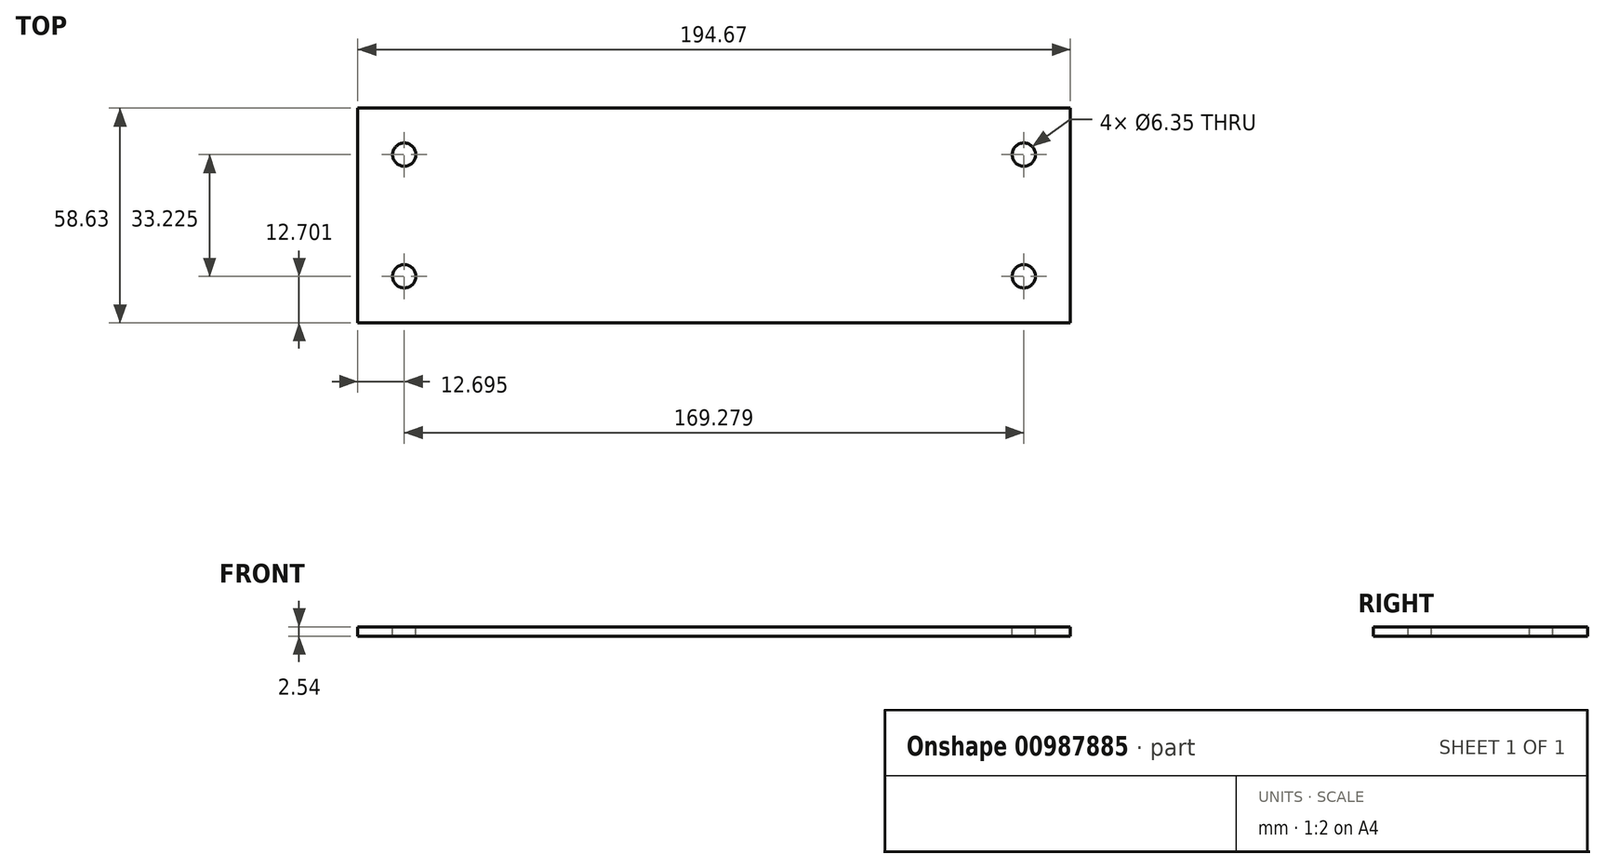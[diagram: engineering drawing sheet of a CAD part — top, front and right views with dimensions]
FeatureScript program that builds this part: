
annotation { "Feature Type Name" : "Feature", "Feature Type Description" : "" }
export const myFeature = defineFeature(function(context is Context, id is Id, definition is map)
    precondition{}
    {
        {
            var Q0;
            Q0=qCreatedBy(makeId("Top.planeOp"),FACE);
            var sketch = newSketch(context, id + "F0", { "sketchPlane" : qUnion([Q0])});
            skLineSegment(sketch, "E0.bottom", {"start": v(-83.6, 39.18) * mm, "end": v(111.07, 39.18) * mm});
            skLineSegment(sketch, "E0.top", {"start": v(-83.6, -19.45) * mm, "end": v(111.07, -19.45) * mm});
            skLineSegment(sketch, "E0.left", {"start": v(-83.6, 39.18) * mm, "end": v(-83.6, -19.45) * mm});
            skLineSegment(sketch, "E0.right", {"start": v(111.07, 39.18) * mm, "end": v(111.07, -19.45) * mm});
            skSolve(sketch);
        }
        {
            var Q0;
            Q0=makeQuery(id+"F0.imprint","IMPRINT",FACE,{"disambiguationData":[TD([[makeQuery(id+"F0.imprint","IMPRINT",EDGE,{"derivedFrom":sQuery(id+"F0.wireOp",EDGE,"E0.bottom")}),-1.0]])]});
            extrude(context, id + "F1", {"entities" : qUnion([Q0]), "depth" : 2.54 * mm, "offsetDistance" : 25.4 * mm});
        }
        {
            var Q0;
            Q0=makeQuery(id+"F1.opExtrude","CAP_FACE",FACE,{"disambiguationData":[OSD([sQuery(id+"F0.wireOp",EDGE,"E0.bottom"),sQuery(id+"F0.wireOp",EDGE,"E0.top"),sQuery(id+"F0.wireOp",EDGE,"E0.left"),sQuery(id+"F0.wireOp",EDGE,"E0.right")])],"isStart":false});
            var sketch = newSketch(context, id + "F2", { "sketchPlane" : qUnion([Q0])});
            skLineSegment(sketch, "E1.bottom", {"start": v(-83.6, 39.18) * mm, "end": v(-70.9, 39.18) * mm});
            skLineSegment(sketch, "E1.top", {"start": v(-83.6, -19.45) * mm, "end": v(-70.9, -19.45) * mm});
            skLineSegment(sketch, "E1.left", {"start": v(-83.6, 39.18) * mm, "end": v(-83.6, -19.45) * mm});
            skLineSegment(sketch, "E1.right", {"start": v(-70.9, 39.18) * mm, "end": v(-70.9, -19.45) * mm});
            skLineSegment(sketch, "E2.bottom", {"start": v(111.07, 39.18) * mm, "end": v(98.37, 39.18) * mm});
            skLineSegment(sketch, "E2.top", {"start": v(111.07, -19.45) * mm, "end": v(98.37, -19.45) * mm});
            skLineSegment(sketch, "E2.left", {"start": v(111.07, 39.18) * mm, "end": v(111.07, -19.45) * mm});
            skLineSegment(sketch, "E2.right", {"start": v(98.37, 39.18) * mm, "end": v(98.37, -19.45) * mm});
            skLineSegment(sketch, "E3.bottom", {"start": v(-83.6, 39.18) * mm, "end": v(111.07, 39.18) * mm});
            skLineSegment(sketch, "E3.top", {"start": v(-83.6, 26.48) * mm, "end": v(111.07, 26.48) * mm});
            skLineSegment(sketch, "E3.left", {"start": v(-83.6, 39.18) * mm, "end": v(-83.6, 26.48) * mm});
            skLineSegment(sketch, "E3.right", {"start": v(111.07, 39.18) * mm, "end": v(111.07, 26.48) * mm});
            skLineSegment(sketch, "E4.bottom", {"start": v(-83.6, -19.45) * mm, "end": v(111.07, -19.45) * mm});
            skLineSegment(sketch, "E4.top", {"start": v(-83.6, -6.75) * mm, "end": v(111.07, -6.75) * mm});
            skLineSegment(sketch, "E4.left", {"start": v(-83.6, -19.45) * mm, "end": v(-83.6, -6.75) * mm});
            skLineSegment(sketch, "E4.right", {"start": v(111.07, -19.45) * mm, "end": v(111.07, -6.75) * mm});
            skCircle(sketch, "E5", {"center": v(-70.9, -6.75) * mm, "radius": 3.18 * mm});
            skCircle(sketch, "E6", {"center": v(-70.9, 26.48) * mm, "radius": 3.18 * mm});
            skCircle(sketch, "E7", {"center": v(98.37, 26.48) * mm, "radius": 3.18 * mm});
            skCircle(sketch, "E8", {"center": v(98.37, -6.75) * mm, "radius": 3.18 * mm});
            skLineSegment(sketch, "E9", {"start": v(13.73, 39.18) * mm, "end": v(13.73, -19.45) * mm});
            skLineSegment(sketch, "E10", {"start": v(-83.6, 9.86) * mm, "end": v(111.07, 9.86) * mm});
            skLineSegment(sketch, "E11", {"start": v(13.73, 9.86) * mm, "end": v(45.48, 9.86) * mm});
            skLineSegment(sketch, "E12", {"start": v(45.48, 9.86) * mm, "end": v(45.48, 35.26) * mm});
            skLineSegment(sketch, "E13", {"start": v(45.48, 35.26) * mm, "end": v(-18.02, 35.26) * mm});
            skLineSegment(sketch, "E14", {"start": v(-18.02, 35.26) * mm, "end": v(-18.02, 0) * mm});
            skLineSegment(sketch, "E15", {"start": v(45.48, 9.86) * mm, "end": v(45.48, -15.54) * mm});
            skLineSegment(sketch, "E16", {"start": v(45.48, -15.54) * mm, "end": v(-18.02, -15.54) * mm});
            skLineSegment(sketch, "E17", {"start": v(-18.02, -15.54) * mm, "end": v(-18.02, 35.26) * mm});
            skSolve(sketch);
        }
        {
            var Q0;
            {var subQ0=sQuery(id+"F2.wireOp",EDGE,"E6");var subQ1=sQuery(id+"F2.wireOp",EDGE,"E1.right");var subQ2=makeQuery(id+"F2.imprint","INTERSECT",VERTEX,{"disambiguationData":[OD(1.0)],"derivedFrom":[subQ1,subQ0]});Q0=makeQuery(id+"F2.imprint","IMPRINT",FACE,{"disambiguationData":[TD([[makeQuery(id+"F2.imprint","IMPRINT",EDGE,{"disambiguationData":[TD([[subQ2,-1.0]])],"derivedFrom":subQ1}),-1.0]])]});}
            var Q1;
            {var subQ0=sQuery(id+"F2.wireOp",EDGE,"E6");var subQ1=sQuery(id+"F2.wireOp",EDGE,"E1.right");var subQ2=makeQuery(id+"F2.imprint","INTERSECT",VERTEX,{"disambiguationData":[OD(1.0)],"derivedFrom":[subQ1,subQ0]});Q1=makeQuery(id+"F2.imprint","IMPRINT",FACE,{"disambiguationData":[TD([[makeQuery(id+"F2.imprint","IMPRINT",EDGE,{"disambiguationData":[TD([[subQ2,-1.0]])],"derivedFrom":subQ1}),1.0]])]});}
            var Q2;
            {var subQ0=sQuery(id+"F2.wireOp",EDGE,"E6");var subQ1=sQuery(id+"F2.wireOp",EDGE,"E1.right");var subQ2=makeQuery(id+"F2.imprint","INTERSECT",VERTEX,{"disambiguationData":[OD(0.0)],"derivedFrom":[subQ1,subQ0]});Q2=makeQuery(id+"F2.imprint","IMPRINT",FACE,{"disambiguationData":[TD([[makeQuery(id+"F2.imprint","IMPRINT",EDGE,{"disambiguationData":[TD([[subQ2,1.0]])],"derivedFrom":subQ1}),1.0]])]});}
            var Q3;
            {var subQ0=sQuery(id+"F2.wireOp",EDGE,"E6");var subQ1=sQuery(id+"F2.wireOp",EDGE,"E1.right");var subQ2=makeQuery(id+"F2.imprint","INTERSECT",VERTEX,{"disambiguationData":[OD(0.0)],"derivedFrom":[subQ1,subQ0]});Q3=makeQuery(id+"F2.imprint","IMPRINT",FACE,{"disambiguationData":[TD([[makeQuery(id+"F2.imprint","IMPRINT",EDGE,{"disambiguationData":[TD([[subQ2,1.0]])],"derivedFrom":subQ1}),-1.0]])]});}
            var Q4;
            {var subQ0=sQuery(id+"F2.wireOp",EDGE,"E5");var subQ1=sQuery(id+"F2.wireOp",EDGE,"E1.right");var subQ2=makeQuery(id+"F2.imprint","INTERSECT",VERTEX,{"disambiguationData":[OD(0.0)],"derivedFrom":[subQ1,subQ0]});Q4=makeQuery(id+"F2.imprint","IMPRINT",FACE,{"disambiguationData":[TD([[makeQuery(id+"F2.imprint","IMPRINT",EDGE,{"disambiguationData":[TD([[subQ2,-1.0]])],"derivedFrom":subQ1}),-1.0]])]});}
            var Q5;
            {var subQ0=sQuery(id+"F2.wireOp",EDGE,"E5");var subQ1=sQuery(id+"F2.wireOp",EDGE,"E1.right");var subQ2=makeQuery(id+"F2.imprint","INTERSECT",VERTEX,{"disambiguationData":[OD(0.0)],"derivedFrom":[subQ1,subQ0]});Q5=makeQuery(id+"F2.imprint","IMPRINT",FACE,{"disambiguationData":[TD([[makeQuery(id+"F2.imprint","IMPRINT",EDGE,{"disambiguationData":[TD([[subQ2,-1.0]])],"derivedFrom":subQ1}),1.0]])]});}
            var Q6;
            {var subQ0=sQuery(id+"F2.wireOp",EDGE,"E5");var subQ1=sQuery(id+"F2.wireOp",EDGE,"E1.right");var subQ2=makeQuery(id+"F2.imprint","INTERSECT",VERTEX,{"disambiguationData":[OD(1.0)],"derivedFrom":[subQ1,subQ0]});Q6=makeQuery(id+"F2.imprint","IMPRINT",FACE,{"disambiguationData":[TD([[makeQuery(id+"F2.imprint","IMPRINT",EDGE,{"disambiguationData":[TD([[subQ2,1.0]])],"derivedFrom":subQ1}),1.0]])]});}
            var Q7;
            {var subQ0=sQuery(id+"F2.wireOp",EDGE,"E5");var subQ1=sQuery(id+"F2.wireOp",EDGE,"E1.right");var subQ2=makeQuery(id+"F2.imprint","INTERSECT",VERTEX,{"disambiguationData":[OD(1.0)],"derivedFrom":[subQ1,subQ0]});Q7=makeQuery(id+"F2.imprint","IMPRINT",FACE,{"disambiguationData":[TD([[makeQuery(id+"F2.imprint","IMPRINT",EDGE,{"disambiguationData":[TD([[subQ2,1.0]])],"derivedFrom":subQ1}),-1.0]])]});}
            var Q8;
            {var subQ0=sQuery(id+"F2.wireOp",EDGE,"E7");var subQ1=sQuery(id+"F2.wireOp",EDGE,"E2.right");var subQ2=makeQuery(id+"F2.imprint","INTERSECT",VERTEX,{"disambiguationData":[OD(1.0)],"derivedFrom":[subQ1,subQ0]});Q8=makeQuery(id+"F2.imprint","IMPRINT",FACE,{"disambiguationData":[TD([[makeQuery(id+"F2.imprint","IMPRINT",EDGE,{"disambiguationData":[TD([[subQ2,-1.0]])],"derivedFrom":subQ1}),-1.0]])]});}
            var Q9;
            {var subQ0=sQuery(id+"F2.wireOp",EDGE,"E7");var subQ1=sQuery(id+"F2.wireOp",EDGE,"E2.right");var subQ2=makeQuery(id+"F2.imprint","INTERSECT",VERTEX,{"disambiguationData":[OD(1.0)],"derivedFrom":[subQ1,subQ0]});Q9=makeQuery(id+"F2.imprint","IMPRINT",FACE,{"disambiguationData":[TD([[makeQuery(id+"F2.imprint","IMPRINT",EDGE,{"disambiguationData":[TD([[subQ2,-1.0]])],"derivedFrom":subQ1}),1.0]])]});}
            var Q10;
            {var subQ0=sQuery(id+"F2.wireOp",EDGE,"E7");var subQ1=sQuery(id+"F2.wireOp",EDGE,"E2.right");var subQ2=makeQuery(id+"F2.imprint","INTERSECT",VERTEX,{"disambiguationData":[OD(0.0)],"derivedFrom":[subQ1,subQ0]});Q10=makeQuery(id+"F2.imprint","IMPRINT",FACE,{"disambiguationData":[TD([[makeQuery(id+"F2.imprint","IMPRINT",EDGE,{"disambiguationData":[TD([[subQ2,1.0]])],"derivedFrom":subQ1}),1.0]])]});}
            var Q11;
            {var subQ0=sQuery(id+"F2.wireOp",EDGE,"E7");var subQ1=sQuery(id+"F2.wireOp",EDGE,"E2.right");var subQ2=makeQuery(id+"F2.imprint","INTERSECT",VERTEX,{"disambiguationData":[OD(0.0)],"derivedFrom":[subQ1,subQ0]});Q11=makeQuery(id+"F2.imprint","IMPRINT",FACE,{"disambiguationData":[TD([[makeQuery(id+"F2.imprint","IMPRINT",EDGE,{"disambiguationData":[TD([[subQ2,1.0]])],"derivedFrom":subQ1}),-1.0]])]});}
            var Q12;
            {var subQ0=sQuery(id+"F2.wireOp",EDGE,"E8");var subQ1=sQuery(id+"F2.wireOp",EDGE,"E2.right");var subQ2=makeQuery(id+"F2.imprint","INTERSECT",VERTEX,{"disambiguationData":[OD(0.0)],"derivedFrom":[subQ1,subQ0]});Q12=makeQuery(id+"F2.imprint","IMPRINT",FACE,{"disambiguationData":[TD([[makeQuery(id+"F2.imprint","IMPRINT",EDGE,{"disambiguationData":[TD([[subQ2,-1.0]])],"derivedFrom":subQ1}),1.0]])]});}
            var Q13;
            {var subQ0=sQuery(id+"F2.wireOp",EDGE,"E8");var subQ1=sQuery(id+"F2.wireOp",EDGE,"E2.right");var subQ2=makeQuery(id+"F2.imprint","INTERSECT",VERTEX,{"disambiguationData":[OD(1.0)],"derivedFrom":[subQ1,subQ0]});Q13=makeQuery(id+"F2.imprint","IMPRINT",FACE,{"disambiguationData":[TD([[makeQuery(id+"F2.imprint","IMPRINT",EDGE,{"disambiguationData":[TD([[subQ2,1.0]])],"derivedFrom":subQ1}),1.0]])]});}
            var Q14;
            {var subQ0=sQuery(id+"F2.wireOp",EDGE,"E8");var subQ1=sQuery(id+"F2.wireOp",EDGE,"E2.right");var subQ2=makeQuery(id+"F2.imprint","INTERSECT",VERTEX,{"disambiguationData":[OD(1.0)],"derivedFrom":[subQ1,subQ0]});Q14=makeQuery(id+"F2.imprint","IMPRINT",FACE,{"disambiguationData":[TD([[makeQuery(id+"F2.imprint","IMPRINT",EDGE,{"disambiguationData":[TD([[subQ2,1.0]])],"derivedFrom":subQ1}),-1.0]])]});}
            var Q15;
            {var subQ0=sQuery(id+"F2.wireOp",EDGE,"E8");var subQ1=sQuery(id+"F2.wireOp",EDGE,"E2.right");var subQ2=makeQuery(id+"F2.imprint","INTERSECT",VERTEX,{"disambiguationData":[OD(0.0)],"derivedFrom":[subQ1,subQ0]});Q15=makeQuery(id+"F2.imprint","IMPRINT",FACE,{"disambiguationData":[TD([[makeQuery(id+"F2.imprint","IMPRINT",EDGE,{"disambiguationData":[TD([[subQ2,-1.0]])],"derivedFrom":subQ1}),-1.0]])]});}
            extrude(context, id + "F3", {"entities" : qUnion([Q0, Q1, Q2, Q3, Q4, Q5, Q6, Q7, Q8, Q9, Q10, Q11, Q12, Q13, Q14, Q15]), "operationType" : NewBodyOperationType.REMOVE, "oppositeDirection" : true, "depth" : 25.4 * mm, "offsetDistance" : 25.4 * mm});
        }
    });
